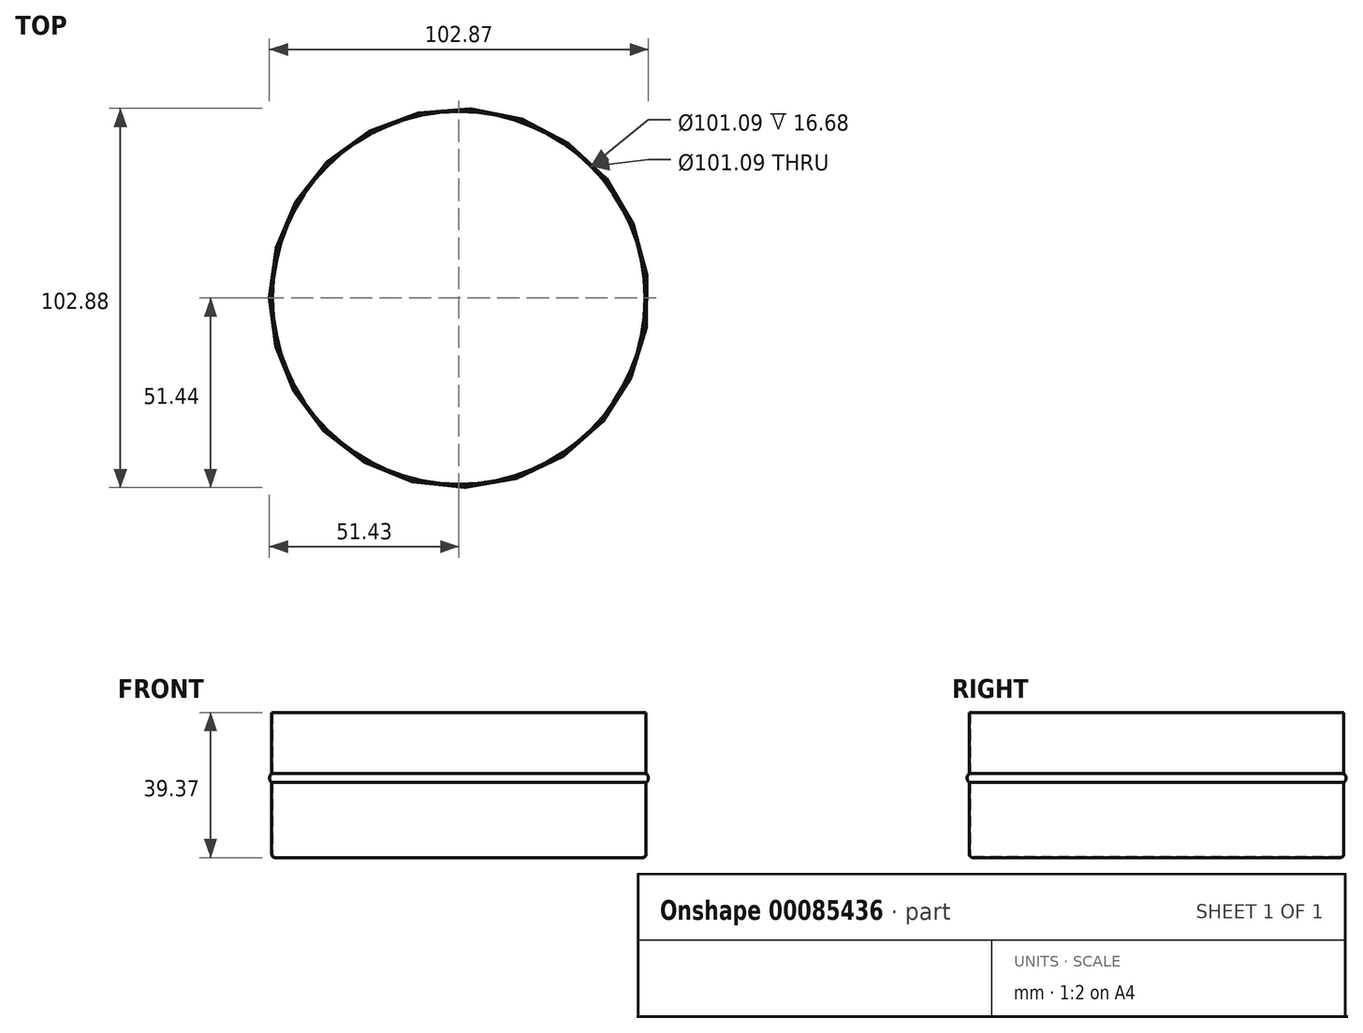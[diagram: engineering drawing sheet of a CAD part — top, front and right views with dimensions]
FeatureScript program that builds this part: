
annotation { "Feature Type Name" : "Feature", "Feature Type Description" : "" }
export const myFeature = defineFeature(function(context is Context, id is Id, definition is map)
    precondition{}
    {
        {
            var Q0;
            Q0=qCreatedBy(makeId("Front.planeOp"),FACE);
            var sketch = newSketch(context, id + "F0", { "sketchPlane" : qUnion([Q0])});
            skLineSegment(sketch, "E0", {"start": v(0, 0) * mm, "end": v(0, 42.74) * mm, "construction": true});
            skLineSegment(sketch, "E1", {"start": v(0, 0) * mm, "end": v(49.91, 0) * mm});
            skLineSegment(sketch, "E2", {"start": v(50.8, 0.89) * mm, "end": v(50.8, 20.35) * mm});
            skArc(sketch, "E3", {"start": v(50.8, 20.35) * mm, "mid": v(51.44, 21.59) * mm, "end": v(50.8, 22.83) * mm});
            skPoint(sketch, "E4", {"position": v(51.44, 21.59) * mm});
            skLineSegment(sketch, "E5.trimOffspring", {"start": v(50.8, 22.83) * mm, "end": v(50.8, 39.37) * mm});
            skPoint(sketch, "E6.visualSharp", {"position": v(50.8, 0) * mm});
            skArc(sketch, "E6.filletArc", {"start": v(49.91, 0) * mm, "mid": v(50.54, 0.26) * mm, "end": v(50.8, 0.89) * mm});
            skLineSegment(sketch, "E7.0", {"start": v(50.55, 22.69) * mm, "end": v(50.55, 39.37) * mm});
            skLineSegment(sketch, "E7.1", {"start": v(0, 0.25) * mm, "end": v(49.91, 0.25) * mm});
            skArc(sketch, "E7.2", {"start": v(49.91, 0.25) * mm, "mid": v(50.36, 0.44) * mm, "end": v(50.55, 0.89) * mm});
            skLineSegment(sketch, "E7.3", {"start": v(50.55, 0.89) * mm, "end": v(50.55, 20.5) * mm});
            skArc(sketch, "E7.4", {"start": v(50.55, 20.5) * mm, "mid": v(51.18, 21.59) * mm, "end": v(50.55, 22.69) * mm});
            skLineSegment(sketch, "E8", {"start": v(50.55, 39.37) * mm, "end": v(50.8, 39.37) * mm});
            skLineSegment(sketch, "E9", {"start": v(0, 0.25) * mm, "end": v(0, 0) * mm});
            skSolve(sketch);
        }
        {
            var Q0;
            Q0 = qSketchRegion(id + "F0", true);
            var Q1;
            Q1=sQuery(id+"F0.wireOp",EDGE,"E0");
            revolve(context, id + "F1", {"entities" : qUnion([Q0]), "axis" : qUnion([Q1]), "revolveType" : RevolveType.FULL});
        }
    });
